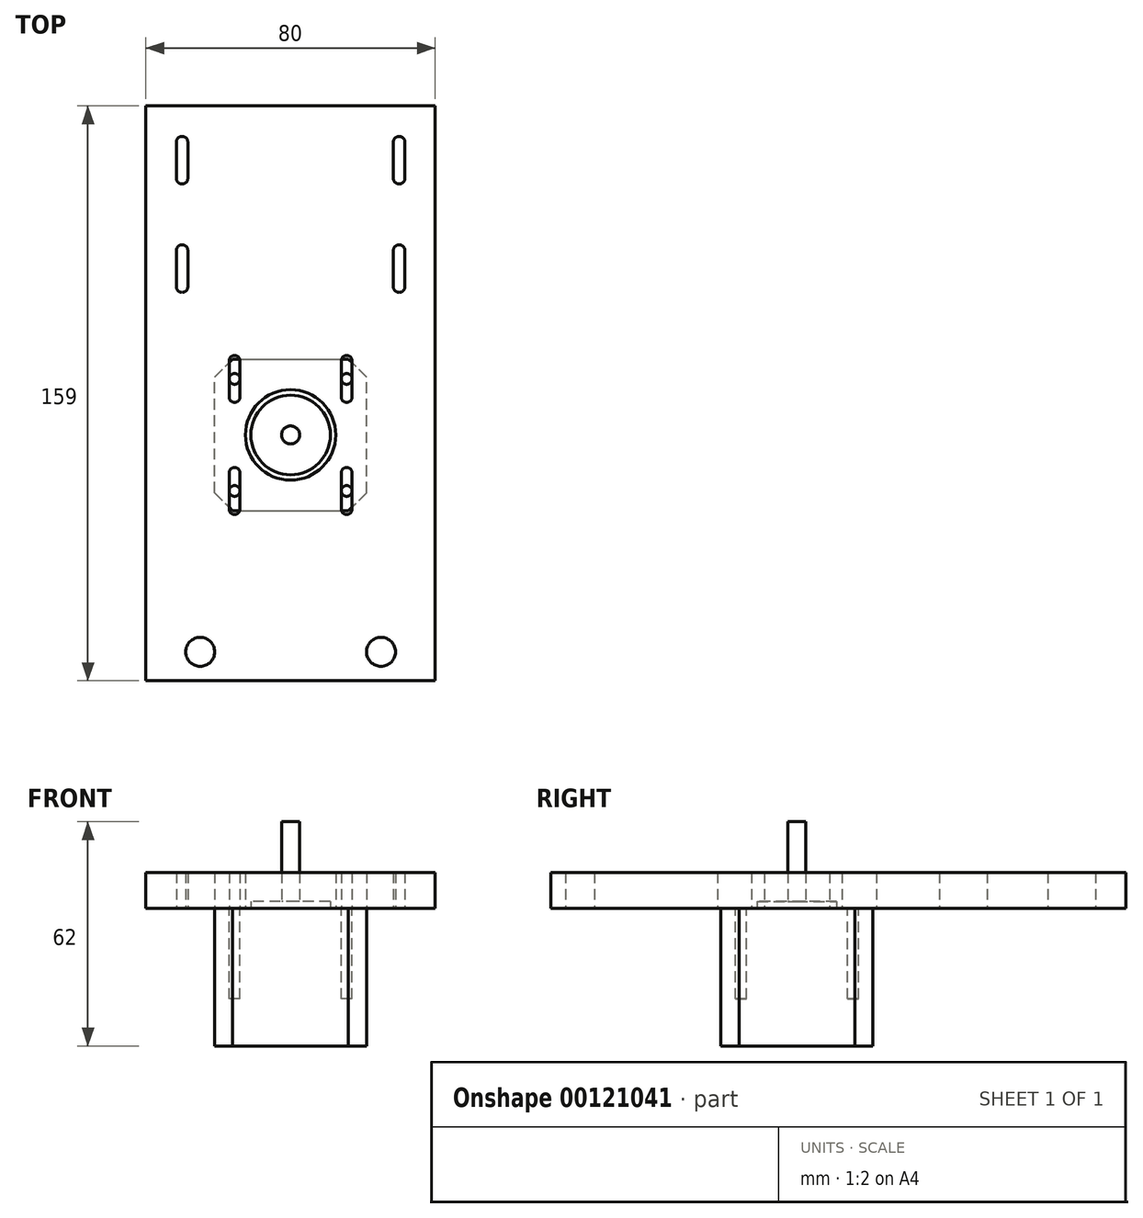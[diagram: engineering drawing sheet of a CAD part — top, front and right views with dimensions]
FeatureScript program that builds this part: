
annotation { "Feature Type Name" : "Feature", "Feature Type Description" : "" }
export const myFeature = defineFeature(function(context is Context, id is Id, definition is map)
    precondition{}
    {
        {
            var Q0;
            Q0=qCreatedBy(makeId("Top.planeOp"),FACE);
            var sketch = newSketch(context, id + "F0", { "sketchPlane" : qUnion([Q0])});
            skLineSegment(sketch, "E0.bottom", {"start": v(0, 0) * mm, "end": v(42, 0) * mm});
            skLineSegment(sketch, "E0.top", {"start": v(0, 42) * mm, "end": v(42, 42) * mm});
            skLineSegment(sketch, "E0.left", {"start": v(0, 0) * mm, "end": v(0, 42) * mm});
            skLineSegment(sketch, "E0.right", {"start": v(42, 0) * mm, "end": v(42, 42) * mm});
            skSolve(sketch);
        }
        {
            var Q0;
            Q0=qSketchRegion(id+"F0",true);
            extrude(context, id + "F1", {"entities" : qUnion([Q0]), "depth" : 38 * mm});
        }
        {
            var Q0;
            Q0=makeQuery(id+"F1.opExtrude","SWEPT_EDGE",EDGE,{"disambiguationData":[OSD([sQuery(id+"F0.wireOp",EDGE,"E0.bottom"),sQuery(id+"F0.wireOp",EDGE,"E0.left")])]});
            var Q1;
            Q1=makeQuery(id+"F1.opExtrude","SWEPT_EDGE",EDGE,{"disambiguationData":[OSD([sQuery(id+"F0.wireOp",EDGE,"E0.top"),sQuery(id+"F0.wireOp",EDGE,"E0.left")])]});
            var Q2;
            Q2=makeQuery(id+"F1.opExtrude","SWEPT_EDGE",EDGE,{"disambiguationData":[OSD([sQuery(id+"F0.wireOp",EDGE,"E0.bottom"),sQuery(id+"F0.wireOp",EDGE,"E0.right")])]});
            var Q3;
            Q3=makeQuery(id+"F1.opExtrude","SWEPT_EDGE",EDGE,{"disambiguationData":[OSD([sQuery(id+"F0.wireOp",EDGE,"E0.top"),sQuery(id+"F0.wireOp",EDGE,"E0.right")])]});
            chamfer(context, id + "F2", {"entities" : qUnion([Q0, Q1, Q2, Q3]), "width" : 5 * mm, "tangentPropagation" : true});
        }
        {
            var Q0;
            Q0=makeQuery(id+"F1.opExtrude","CAP_FACE",FACE,{"disambiguationData":[OSD([sQuery(id+"F0.wireOp",EDGE,"E0.bottom"),sQuery(id+"F0.wireOp",EDGE,"E0.top"),sQuery(id+"F0.wireOp",EDGE,"E0.left"),sQuery(id+"F0.wireOp",EDGE,"E0.right")])],"isStart":false});
            var sketch = newSketch(context, id + "F3", { "sketchPlane" : qUnion([Q0])});
            skCircle(sketch, "E1", {"center": v(21, 21) * mm, "radius": 11 * mm});
            skSolve(sketch);
        }
        {
            var Q0;
            Q0=qSketchRegion(id+"F3",true);
            extrude(context, id + "F4", {"entities" : qUnion([Q0]), "operationType" : NewBodyOperationType.ADD, "depth" : 2 * mm});
        }
        {
            var Q0;
            Q0=makeQuery(id+"F4.opExtrude","CAP_FACE",FACE,{"disambiguationData":[OSD([sQuery(id+"F3.wireOp",EDGE,"E1")])],"isStart":false});
            var sketch = newSketch(context, id + "F5", { "sketchPlane" : qUnion([Q0])});
            skCircle(sketch, "E2", {"center": v(21, 21) * mm, "radius": 2.5 * mm});
            skSolve(sketch);
        }
        {
            var Q0;
            Q0=qSketchRegion(id+"F5",true);
            extrude(context, id + "F6", {"entities" : qUnion([Q0]), "operationType" : NewBodyOperationType.ADD, "depth" : 22 * mm});
        }
        {
            var Q0;
            Q0=makeQuery(id+"F1.opExtrude","CAP_FACE",FACE,{"disambiguationData":[OSD([sQuery(id+"F0.wireOp",EDGE,"E0.bottom"),sQuery(id+"F0.wireOp",EDGE,"E0.top"),sQuery(id+"F0.wireOp",EDGE,"E0.left"),sQuery(id+"F0.wireOp",EDGE,"E0.right")])],"isStart":false});
            var sketch = newSketch(context, id + "F7", { "sketchPlane" : qUnion([Q0])});
            skCircle(sketch, "E3", {"center": v(5.5, 36.5) * mm, "radius": 1.5 * mm});
            skCircle(sketch, "E4", {"center": v(5.5, 5.5) * mm, "radius": 1.5 * mm});
            skCircle(sketch, "E5", {"center": v(36.5, 36.5) * mm, "radius": 1.5 * mm});
            skCircle(sketch, "E6", {"center": v(36.5, 5.5) * mm, "radius": 1.5 * mm});
            skSolve(sketch);
        }
        {
            var Q0;
            Q0=qSketchRegion(id+"F7",true);
            extrude(context, id + "F8", {"entities" : qUnion([Q0]), "operationType" : NewBodyOperationType.REMOVE, "oppositeDirection" : true, "depth" : 25 * mm});
        }
        {
            var Q0;
            Q0=makeQuery(id+"F1.opExtrude","CAP_FACE",FACE,{"disambiguationData":[OSD([sQuery(id+"F0.wireOp",EDGE,"E0.bottom"),sQuery(id+"F0.wireOp",EDGE,"E0.top"),sQuery(id+"F0.wireOp",EDGE,"E0.left"),sQuery(id+"F0.wireOp",EDGE,"E0.right")])],"isStart":false});
            var sketch = newSketch(context, id + "F9", { "sketchPlane" : qUnion([Q0])});
            skCircle(sketch, "E7.0", {"center": v(5.5, 36.5) * mm, "radius": 1.5 * mm, "construction": true});
            skCircle(sketch, "E8.0", {"center": v(36.5, 36.5) * mm, "radius": 1.5 * mm, "construction": true});
            skCircle(sketch, "E9.0", {"center": v(36.5, 5.5) * mm, "radius": 1.5 * mm, "construction": true});
            skCircle(sketch, "E10.0", {"center": v(5.5, 5.5) * mm, "radius": 1.5 * mm, "construction": true});
            skLineSegment(sketch, "E11", {"start": v(21, 42) * mm, "end": v(21, 0) * mm, "construction": true});
            skLineSegment(sketch, "E12", {"start": v(0, 21) * mm, "end": v(42, 21) * mm, "construction": true});
            skLineSegment(sketch, "E13", {"start": v(4, 41.5) * mm, "end": v(4, 31.5) * mm});
            skPoint(sketch, "E14", {"position": v(4, 36.5) * mm});
            skLineSegment(sketch, "E15", {"start": v(5.5, 38) * mm, "end": v(5.5, 35) * mm, "construction": true});
            skLineSegment(sketch, "E16.MirrorCS", {"start": v(7, 41.5) * mm, "end": v(7, 31.5) * mm});
            skArc(sketch, "E17", {"start": v(7, 41.5) * mm, "mid": v(5.5, 43) * mm, "end": v(4, 41.5) * mm});
            skArc(sketch, "E18", {"start": v(4, 31.5) * mm, "mid": v(5.5, 30) * mm, "end": v(7, 31.5) * mm});
            skLineSegment(sketch, "E19.MirrorCS", {"start": v(35, 41.5) * mm, "end": v(35, 31.5) * mm});
            skArc(sketch, "E20.MirrorCS", {"start": v(38, 31.5) * mm, "mid": v(36.5, 30) * mm, "end": v(35, 31.5) * mm});
            skLineSegment(sketch, "E21.MirrorCS", {"start": v(38, 41.5) * mm, "end": v(38, 31.5) * mm});
            skPoint(sketch, "E22.MirrorP", {"position": v(38, 36.5) * mm});
            skLineSegment(sketch, "E23.MirrorCS", {"start": v(36.5, 38) * mm, "end": v(36.5, 35) * mm, "construction": true});
            skArc(sketch, "E24.MirrorCS", {"start": v(35, 41.5) * mm, "mid": v(36.5, 43) * mm, "end": v(38, 41.5) * mm});
            skLineSegment(sketch, "E25.MirrorCS", {"start": v(5.5, 4) * mm, "end": v(5.5, 7) * mm, "construction": true});
            skLineSegment(sketch, "E26.MirrorCS", {"start": v(36.5, 4) * mm, "end": v(36.5, 7) * mm, "construction": true});
            skLineSegment(sketch, "E27.MirrorCS", {"start": v(38, 0.5) * mm, "end": v(38, 10.5) * mm});
            skLineSegment(sketch, "E28.MirrorCS", {"start": v(4, 0.5) * mm, "end": v(4, 10.5) * mm});
            skArc(sketch, "E29.MirrorCS", {"start": v(7, 0.5) * mm, "mid": v(5.5, -1) * mm, "end": v(4, 0.5) * mm});
            skLineSegment(sketch, "E30.MirrorCS", {"start": v(35, 0.5) * mm, "end": v(35, 10.5) * mm});
            skArc(sketch, "E31.MirrorCS", {"start": v(4, 10.5) * mm, "mid": v(5.5, 12) * mm, "end": v(7, 10.5) * mm});
            skLineSegment(sketch, "E32.MirrorCS", {"start": v(7, 0.5) * mm, "end": v(7, 10.5) * mm});
            skPoint(sketch, "E33.MirrorP", {"position": v(4, 5.5) * mm});
            skArc(sketch, "E34.MirrorCS", {"start": v(35, 0.5) * mm, "mid": v(36.5, -1) * mm, "end": v(38, 0.5) * mm});
            skPoint(sketch, "E35.MirrorP", {"position": v(38, 5.5) * mm});
            skArc(sketch, "E36.MirrorCS", {"start": v(38, 10.5) * mm, "mid": v(36.5, 12) * mm, "end": v(35, 10.5) * mm});
            skLineSegment(sketch, "E37.MirrorCS", {"start": v(21, 0) * mm, "end": v(21, 42) * mm, "construction": true});
            skLineSegment(sketch, "E38", {"start": v(-19, 112) * mm, "end": v(-19, -47) * mm});
            skLineSegment(sketch, "E39.MirrorCS", {"start": v(61, 112) * mm, "end": v(61, -47) * mm});
            skLineSegment(sketch, "E40", {"start": v(-19, 112) * mm, "end": v(61, 112) * mm});
            skLineSegment(sketch, "E41", {"start": v(61, -47) * mm, "end": v(-19, -47) * mm});
            skCircle(sketch, "E42", {"center": v(-4, -39) * mm, "radius": 4 * mm});
            skCircle(sketch, "E43.MirrorC", {"center": v(46, -39) * mm, "radius": 4 * mm});
            skCircle(sketch, "E44", {"center": v(-4, -39) * mm, "radius": 11 * mm, "construction": true});
            skCircle(sketch, "E45.MirrorC", {"center": v(46, -39) * mm, "radius": 11 * mm, "construction": true});
            skCircle(sketch, "E46.0", {"center": v(21, 21) * mm, "radius": 11 * mm, "construction": true});
            skCircle(sketch, "E47", {"center": v(21, 21) * mm, "radius": 12.5 * mm});
            skLineSegment(sketch, "E48", {"start": v(-10.59, 102) * mm, "end": v(-10.59, 92) * mm});
            skLineSegment(sketch, "E49", {"start": v(-7.4, 102) * mm, "end": v(-7.4, 92) * mm});
            skArc(sketch, "E50", {"start": v(-7.4, 102) * mm, "mid": v(-9, 103.6) * mm, "end": v(-10.59, 102) * mm});
            skArc(sketch, "E51", {"start": v(-10.59, 92) * mm, "mid": v(-9, 90.41) * mm, "end": v(-7.4, 92) * mm});
            skArc(sketch, "E52.0.1.0", {"start": v(-7.4, 72) * mm, "mid": v(-9, 73.6) * mm, "end": v(-10.59, 72) * mm});
            skArc(sketch, "E52.0.1.1", {"start": v(-10.59, 62) * mm, "mid": v(-9, 60.41) * mm, "end": v(-7.4, 62) * mm});
            skLineSegment(sketch, "E52.0.1.2", {"start": v(-10.59, 72) * mm, "end": v(-10.59, 62) * mm});
            skLineSegment(sketch, "E52.0.1.3", {"start": v(-7.4, 72) * mm, "end": v(-7.4, 62) * mm});
            skArc(sketch, "E52.1.0.0", {"start": v(52.59, 102) * mm, "mid": v(51, 103.6) * mm, "end": v(49.4, 102) * mm});
            skArc(sketch, "E52.1.0.1", {"start": v(49.4, 92) * mm, "mid": v(51, 90.41) * mm, "end": v(52.59, 92) * mm});
            skLineSegment(sketch, "E52.1.0.2", {"start": v(49.4, 102) * mm, "end": v(49.4, 92) * mm});
            skLineSegment(sketch, "E52.1.0.3", {"start": v(52.59, 102) * mm, "end": v(52.59, 92) * mm});
            skArc(sketch, "E52.1.1.0", {"start": v(52.59, 72) * mm, "mid": v(51, 73.6) * mm, "end": v(49.4, 72) * mm});
            skArc(sketch, "E52.1.1.1", {"start": v(49.4, 62) * mm, "mid": v(51, 60.41) * mm, "end": v(52.59, 62) * mm});
            skLineSegment(sketch, "E52.1.1.2", {"start": v(49.4, 72) * mm, "end": v(49.4, 62) * mm});
            skLineSegment(sketch, "E52.1.1.3", {"start": v(52.59, 72) * mm, "end": v(52.59, 62) * mm});
            skLineSegment(sketch, "E52.direction1", {"start": v(-9, 102) * mm, "end": v(51, 102) * mm, "construction": true});
            skLineSegment(sketch, "E52.direction2", {"start": v(-9, 102) * mm, "end": v(-9, 72) * mm, "construction": true});
            skSolve(sketch);
        }
        {
            var Q0;
            Q0 = qSketchRegion(id + "F9", true);
            extrude(context, id + "F10", {"entities" : qUnion([Q0]), "depth" : 10 * mm});
        }
    });
